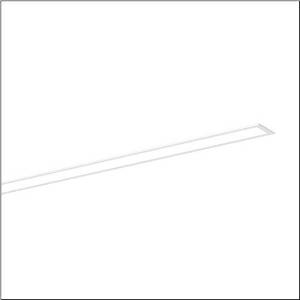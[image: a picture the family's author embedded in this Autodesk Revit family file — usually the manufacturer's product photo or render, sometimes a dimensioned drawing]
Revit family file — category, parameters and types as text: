
# Revit family: silica_r__21_51mx10da32wb_2fdc
name_source: partatom
category: Lighting Fixtures
units: mm (PartAtom-declared; Revit-internal decimal feet)

## family parameters
Cut with Voids When Loaded = No
Host = Face
Light Source = No
Part Type = Normal
Room Calculation Point = No
Round Connector Dimension = Use Diameter
Shared = No

## types (1)
- --- (1 x LED, 2400 lm, 16.1 W, 3000K)
    Apparent Load = 16 VA
    CIE Flux Codes = 48 79 96 100 100
    Color Rendering = 80
    Color Temperature = 3000K
    Default Elevation = 1800 mm
    Description = Silica® 21, office luminaire, primary optical cover: cover, of PMMA, opal, light emission: direct distribution, primary light characteristic: symmetric, installation type: recessed, LED, rated luminous flux: 2.400lm, luminous efficacy: 149lm/W, light colour: 830, colour temperature: 3000K, control gear: DALI 2, with terminal, 3+2-pole, max. 2.5mm², mains connection: 220..240V, AC, 50/60Hz, rated input power: 16.1W, luminaire housing, of aluminium, traffic white (RAL 9016), length: 1.228mm, width: 79mm, height: 53mm, protection rating (complete): IP20, insulation class (complete): insulation class I (protective earthing), certification: CE, ENEC, VDE, permissible operating ambient temperature: 0..+35°C, standard: EN 50419, packaging unit: 1 piece
    Height = 0 mm  [stored 0 ft]
    Lamp = 1 x LED
    Lamp Light Flux = 2400 lm
    Lamp Power = 16.1 W
    Lamp count = 1
    Length = 1227 mm
    Luminous efficacy = 149 lm/W
    Manufacturer = Siteco
    ModVariant = No
    Model = 51MX10DA32WB
    Mounting Place = Ceiling
    Mounting Type = Recessed
    Number of Poles = 1
    OnlyDefault = Yes
    Power Factor = 1
    Product Name = Silica® 21
    Product group = office luminaire | ceiling recessed
    ProductGroupID = 401
    Protection Class = Protection class I
    Protection Degree = IP 20
    RLX_Detail_Level = 1
    RLX_Emergency_Light_Flux = 0 lm
    RLX_Emergency_Type = 0
    RLX_Emergency_Type_DB = No
    RlxData = <blob elided: 21001 chars, md5=6fad62d6>
    Socket = socket
    Standby Power = 0 W
    System Light Flux = 2400 lm
    System Power = 16 W
    Type Comments = factory setting: luminous flux: 100 % | dim-lin: 254 | 233 mA
    Type Image = l_1335891.jpg
    URL = http://relux.com
    VarID = @adj_007423
    Voltage = 0 V
    Weight = 0.00 kg
    Width = 79 mm

note: [stored X ft] marks values corroborated as IEEE doubles in the binary element streams (Revit-internal decimal feet)

## geometry (parser evidence)
native form markers: Blend x4, Sweep x9
no freeform markers — native parametric forms only
